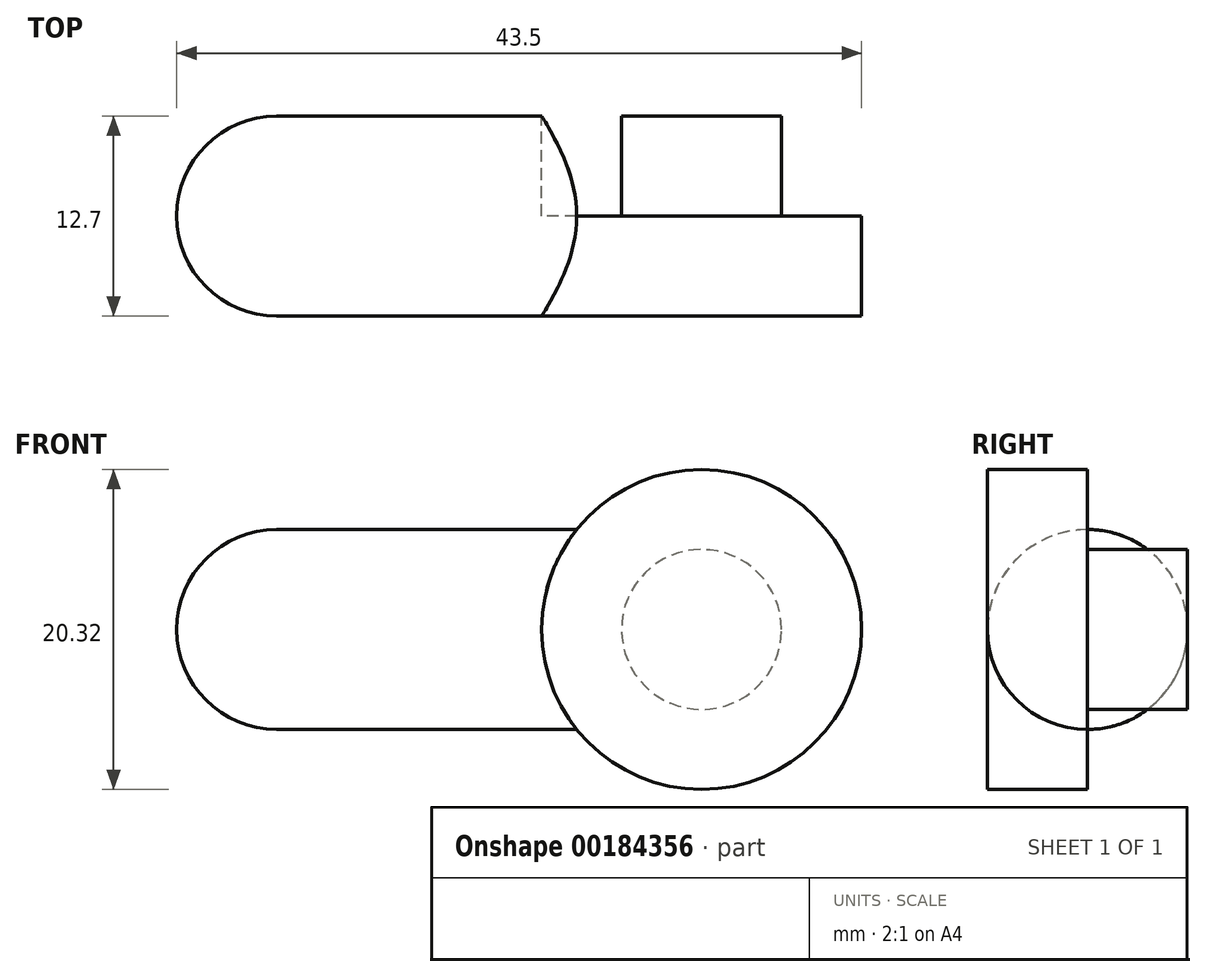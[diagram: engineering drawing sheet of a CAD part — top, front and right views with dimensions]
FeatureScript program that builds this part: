
annotation { "Feature Type Name" : "Feature", "Feature Type Description" : "" }
export const myFeature = defineFeature(function(context is Context, id is Id, definition is map)
    precondition{}
    {
        {
            var Q0;
            Q0=qCreatedBy(makeId("Front.planeOp"),FACE);
            var sketch = newSketch(context, id + "F0", { "sketchPlane" : qUnion([Q0])});
            skLineSegment(sketch, "E0.bottom", {"start": v(-9.53, 6.35) * mm, "end": v(9.53, 6.35) * mm});
            skLineSegment(sketch, "E0.top", {"start": v(-9.53, -6.35) * mm, "end": v(9.53, -6.35) * mm});
            skLineSegment(sketch, "E0.left", {"start": v(-9.53, 6.35) * mm, "end": v(-9.53, -6.35) * mm});
            skLineSegment(sketch, "E0.right", {"start": v(9.53, 6.35) * mm, "end": v(9.53, -6.35) * mm});
            skPoint(sketch, "E0.middle", {"position": v(0, 0) * mm});
            skCircle(sketch, "E1", {"center": v(17.46, 0) * mm, "radius": 10.16 * mm});
            skPoint(sketch, "E1.third.point", {"position": v(27.62, 0) * mm});
            skPoint(sketch, "E2.third.point.positionSnap0", {"position": v(-9.53, 0) * mm});
            skCircle(sketch, "E3", {"center": v(17.46, 0) * mm, "radius": 5.08 * mm});
            skArc(sketch, "E4", {"start": v(-9.53, 6.35) * mm, "mid": v(-15.88, 0) * mm, "end": v(-9.53, -6.35) * mm});
            skSolve(sketch);
        }
        {
            var Q0;
            {var subQ0=sQuery(id+"F0.wireOp",EDGE,"E0.bottom");Q0=makeQuery(id+"F0.imprint","IMPRINT",FACE,{"disambiguationData":[TD([[makeQuery(id+"F0.imprint","IMPRINT",EDGE,{"derivedFrom":subQ0}),-1.0]])]});}
            var Q1;
            Q1=makeQuery(id+"F0.imprint","IMPRINT",FACE,{"disambiguationData":[TD([[makeQuery(id+"F0.imprint","IMPRINT",EDGE,{"derivedFrom":sQuery(id+"F0.wireOp",EDGE,"E0.left")}),-1.0]])]});
            extrude(context, id + "F1", {"entities" : qUnion([Q0, Q1]), "endBound" : BoundingType.SYMMETRIC, "depth" : 12.7 * mm});
        }
        {
            var Q0;
            Q0=makeQuery(id+"F1.opExtrude","CAP_EDGE",EDGE,{"disambiguationData":[OSD([sQuery(id+"F0.wireOp",EDGE,"E0.bottom")])],"isStart":false});
            var Q1;
            Q1=makeQuery(id+"F1.opExtrude","CAP_EDGE",EDGE,{"disambiguationData":[OSD([sQuery(id+"F0.wireOp",EDGE,"E0.bottom")])],"isStart":true});
            var Q2;
            Q2=makeQuery(id+"F1.opExtrude","CAP_EDGE",EDGE,{"disambiguationData":[OSD([sQuery(id+"F0.wireOp",EDGE,"E0.top")])],"isStart":false});
            var Q3;
            Q3=makeQuery(id+"F1.opExtrude","CAP_EDGE",EDGE,{"disambiguationData":[OSD([sQuery(id+"F0.wireOp",EDGE,"E0.top")])],"isStart":true});
            fillet(context, id + "F2", {"entities" : qUnion([Q0, Q1, Q2, Q3]), "radius" : 6.35 * mm, "tangentPropagation" : true, "allowEdgeOverflow" : false});
        }
        {
            var Q0;
            {var subQ0=sQuery(id+"F0.wireOp",EDGE,"E0.right");Q0=makeQuery(id+"F0.imprint","IMPRINT",FACE,{"disambiguationData":[TD([[makeQuery(id+"F0.imprint","IMPRINT",EDGE,{"derivedFrom":subQ0}),1.0]])]});}
            var Q1;
            {var subQ0=sQuery(id+"F0.wireOp",EDGE,"E0.right");Q1=makeQuery(id+"F0.imprint","IMPRINT",FACE,{"disambiguationData":[TD([[makeQuery(id+"F0.imprint","IMPRINT",EDGE,{"derivedFrom":subQ0}),-1.0]])]});}
            extrude(context, id + "F3", {"entities" : qUnion([Q0, Q1]), "operationType" : NewBodyOperationType.ADD, "depth" : 6.35 * mm});
        }
        {
            var Q0;
            Q0=makeQuery(id+"F0.imprint","IMPRINT",FACE,{"disambiguationData":[TD([[makeQuery(id+"F0.imprint","IMPRINT",EDGE,{"derivedFrom":sQuery(id+"F0.wireOp",EDGE,"E3")}),1.0]])]});
            extrude(context, id + "F4", {"entities" : qUnion([Q0]), "operationType" : NewBodyOperationType.ADD, "endBound" : BoundingType.SYMMETRIC, "depth" : 12.7 * mm});
        }
    });
